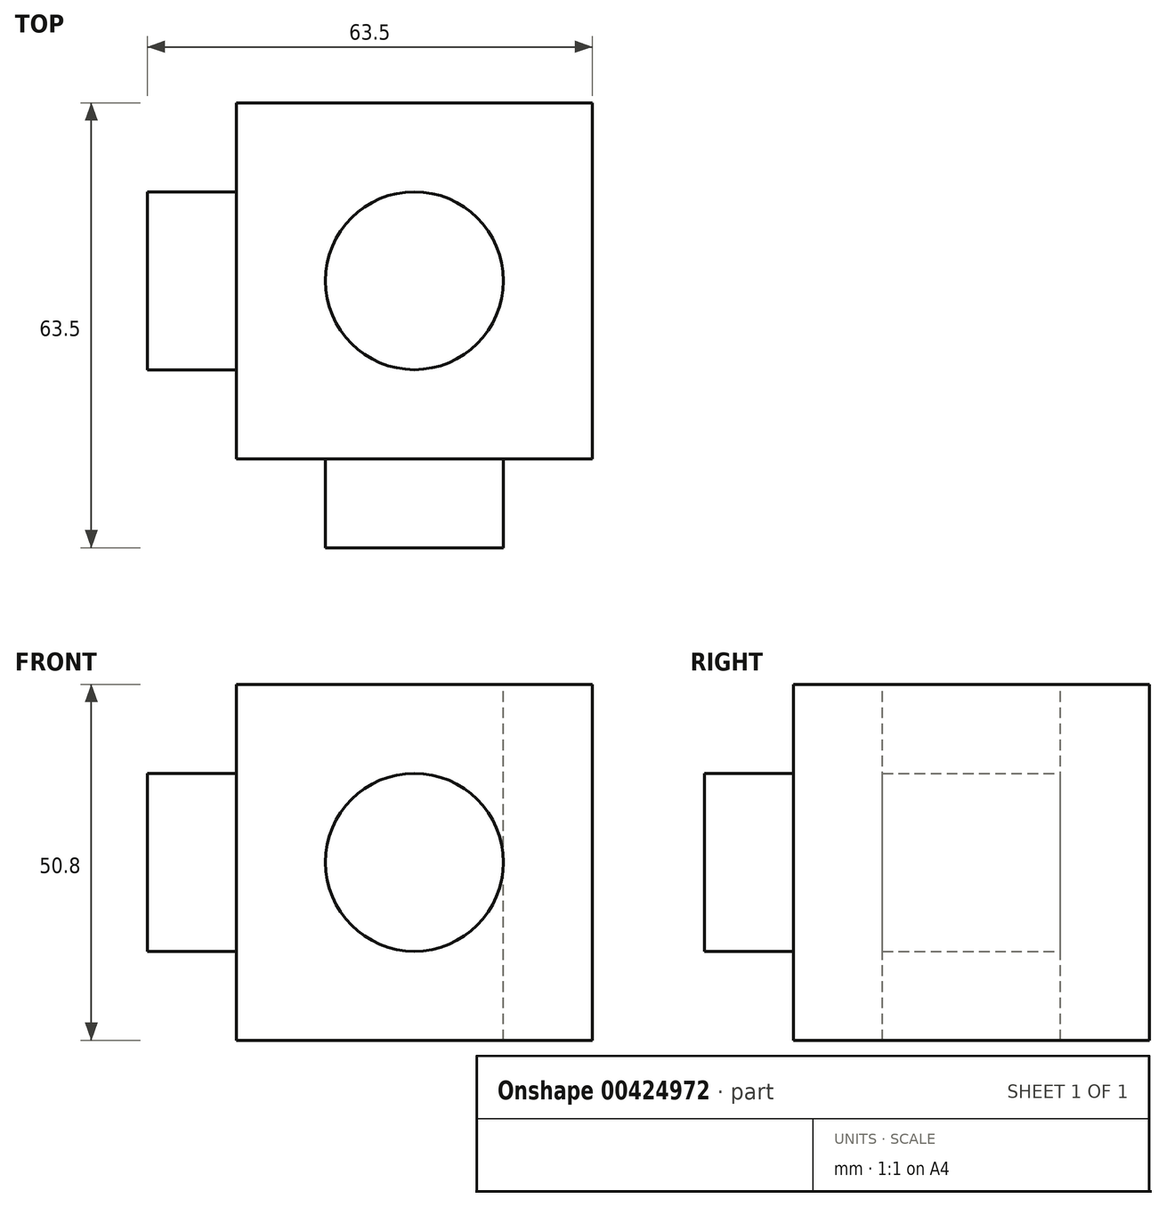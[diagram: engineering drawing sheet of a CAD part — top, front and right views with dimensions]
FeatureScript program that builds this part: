
annotation { "Feature Type Name" : "Feature", "Feature Type Description" : "" }
export const myFeature = defineFeature(function(context is Context, id is Id, definition is map)
    precondition{}
    {
        {
            var Q0;
            Q0=qCreatedBy(makeId("Front.planeOp"),FACE);
            var sketch = newSketch(context, id + "F0", { "sketchPlane" : qUnion([Q0])});
            skLineSegment(sketch, "E0.bottom", {"start": v(0, 0) * mm, "end": v(-50.8, 0) * mm});
            skLineSegment(sketch, "E0.top", {"start": v(0, 50.8) * mm, "end": v(-50.8, 50.8) * mm});
            skLineSegment(sketch, "E0.left", {"start": v(0, 0) * mm, "end": v(0, 50.8) * mm});
            skLineSegment(sketch, "E0.right", {"start": v(-50.8, 0) * mm, "end": v(-50.8, 50.8) * mm});
            skSolve(sketch);
        }
        {
            var Q0;
            Q0=makeQuery(id+"F0.imprint","IMPRINT",FACE,{"disambiguationData":[TD([[makeQuery(id+"F0.imprint","IMPRINT",EDGE,{"derivedFrom":sQuery(id+"F0.wireOp",EDGE,"E0.bottom")}),-1.0]])]});
            extrude(context, id + "F1", {"entities" : qUnion([Q0]), "depth" : 50.8 * mm});
        }
        {
            var Q0;
            Q0=makeQuery(id+"F1.opExtrude","CAP_FACE",FACE,{"disambiguationData":[OSD([sQuery(id+"F0.wireOp",EDGE,"E0.bottom"),sQuery(id+"F0.wireOp",EDGE,"E0.top"),sQuery(id+"F0.wireOp",EDGE,"E0.left"),sQuery(id+"F0.wireOp",EDGE,"E0.right")])],"isStart":false});
            var sketch = newSketch(context, id + "F2", { "sketchPlane" : qUnion([Q0])});
            skCircle(sketch, "E1", {"center": v(-25.4, 25.4) * mm, "radius": 12.7 * mm});
            skSolve(sketch);
        }
        {
            var Q0;
            Q0 = qSketchRegion(id + "F2", true);
            extrude(context, id + "F3", {"entities" : qUnion([Q0]), "operationType" : NewBodyOperationType.ADD, "depth" : 12.7 * mm});
        }
        {
            var Q0;
            Q0=makeQuery(id+"F1.opExtrude","SWEPT_FACE",FACE,{"disambiguationData":[OSD([sQuery(id+"F0.wireOp",EDGE,"E0.top")])]});
            var sketch = newSketch(context, id + "F4", { "sketchPlane" : qUnion([Q0])});
            skCircle(sketch, "E2", {"center": v(-25.4, -25.4) * mm, "radius": 12.7 * mm});
            skSolve(sketch);
        }
        {
            var Q0;
            Q0=makeQuery(id+"F4.imprint","IMPRINT",FACE,{"disambiguationData":[TD([[makeQuery(id+"F4.imprint","IMPRINT",EDGE,{"derivedFrom":sQuery(id+"F4.wireOp",EDGE,"E2")}),1.0]])]});
            extrude(context, id + "F5", {"entities" : qUnion([Q0]), "operationType" : NewBodyOperationType.REMOVE, "oppositeDirection" : true, "depth" : 50.8 * mm});
        }
        {
            var Q0;
            Q0=makeQuery(id+"F1.opExtrude","SWEPT_FACE",FACE,{"disambiguationData":[OSD([sQuery(id+"F0.wireOp",EDGE,"E0.right")])]});
            var sketch = newSketch(context, id + "F6", { "sketchPlane" : qUnion([Q0])});
            skLineSegment(sketch, "E3.bottom", {"start": v(38.1, 12.7) * mm, "end": v(12.7, 12.7) * mm});
            skLineSegment(sketch, "E3.top", {"start": v(38.1, 38.1) * mm, "end": v(12.7, 38.1) * mm});
            skLineSegment(sketch, "E3.left", {"start": v(38.1, 12.7) * mm, "end": v(38.1, 38.1) * mm});
            skLineSegment(sketch, "E3.right", {"start": v(12.7, 12.7) * mm, "end": v(12.7, 38.1) * mm});
            skSolve(sketch);
        }
        {
            var Q0;
            Q0=makeQuery(id+"F6.imprint","IMPRINT",FACE,{"disambiguationData":[TD([[makeQuery(id+"F6.imprint","IMPRINT",EDGE,{"derivedFrom":sQuery(id+"F6.wireOp",EDGE,"E3.bottom")}),-1.0]])]});
            extrude(context, id + "F7", {"entities" : qUnion([Q0]), "operationType" : NewBodyOperationType.ADD, "depth" : 12.7 * mm});
        }
    });
